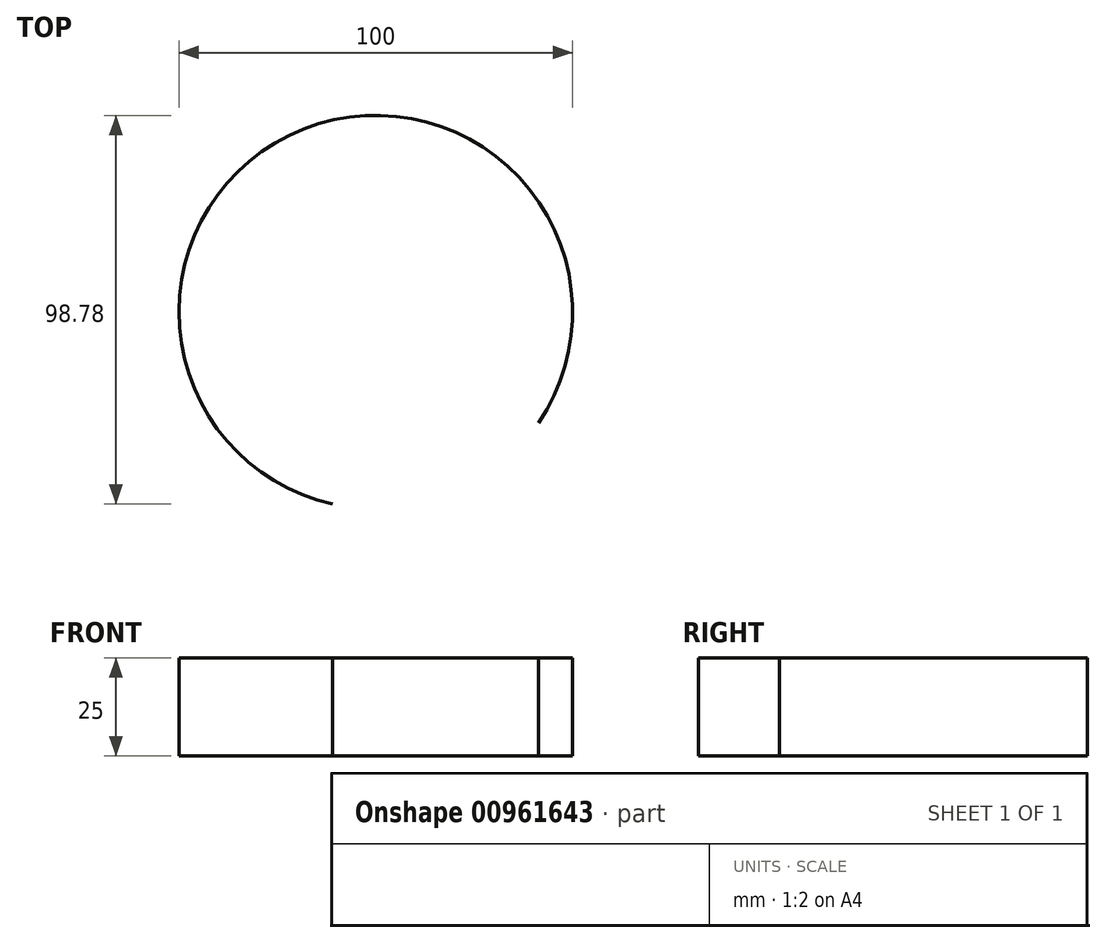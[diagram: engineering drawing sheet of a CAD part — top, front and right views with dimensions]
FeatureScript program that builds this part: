
annotation { "Feature Type Name" : "Feature", "Feature Type Description" : "" }
export const myFeature = defineFeature(function(context is Context, id is Id, definition is map)
    precondition{}
    {
        {
            var Q0;
            Q0=qCreatedBy(makeId("Top.planeOp"),FACE);
            var sketch = newSketch(context, id + "F0", { "sketchPlane" : qUnion([Q0])});
            skArc(sketch, "E0", {"start": v(0, 0) * mm, "mid": v(-59.64, 74.7) * mm, "end": v(-52.3, -20.6) * mm});
            skSolve(sketch);
        }
        {
            var Q0;
            Q0=sQuery(id+"F0.wireOp",EDGE,"E0");
            extrude(context, id + "F1", {"bodyType" : ToolBodyType.SURFACE, "surfaceEntities" : qUnion([Q0]), "depth" : 25 * mm, "offsetDistance" : 25 * mm});
        }
    });
